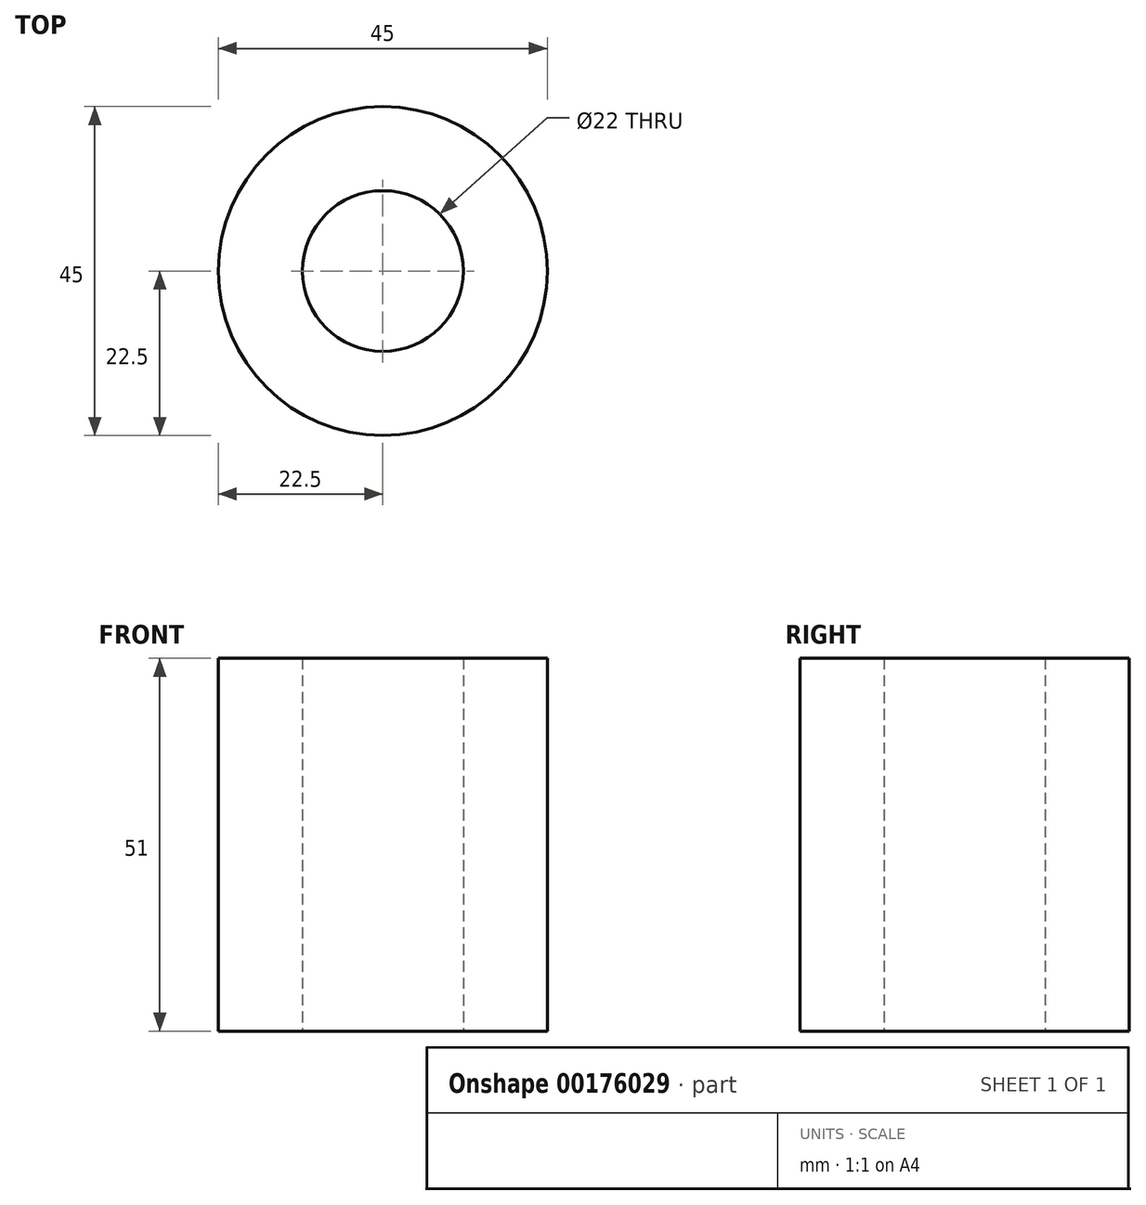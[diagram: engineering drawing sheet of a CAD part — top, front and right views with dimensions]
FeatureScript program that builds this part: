
annotation { "Feature Type Name" : "Feature", "Feature Type Description" : "" }
export const myFeature = defineFeature(function(context is Context, id is Id, definition is map)
    precondition{}
    {
        {
            var Q0;
            Q0=qCreatedBy(makeId("Top.planeOp"),FACE);
            var sketch = newSketch(context, id + "F0", { "sketchPlane" : qUnion([Q0])});
            skCircle(sketch, "E0", {"center": v(0, 0) * mm, "radius": 22.5 * mm});
            skCircle(sketch, "E1", {"center": v(0, 0) * mm, "radius": 11 * mm});
            skSolve(sketch);
        }
        {
            var Q0;
            Q0 = qSketchRegion(id + "F0", true);
            extrude(context, id + "F1", {"entities" : qUnion([Q0]), "depth" : 51 * mm});
        }
    });
